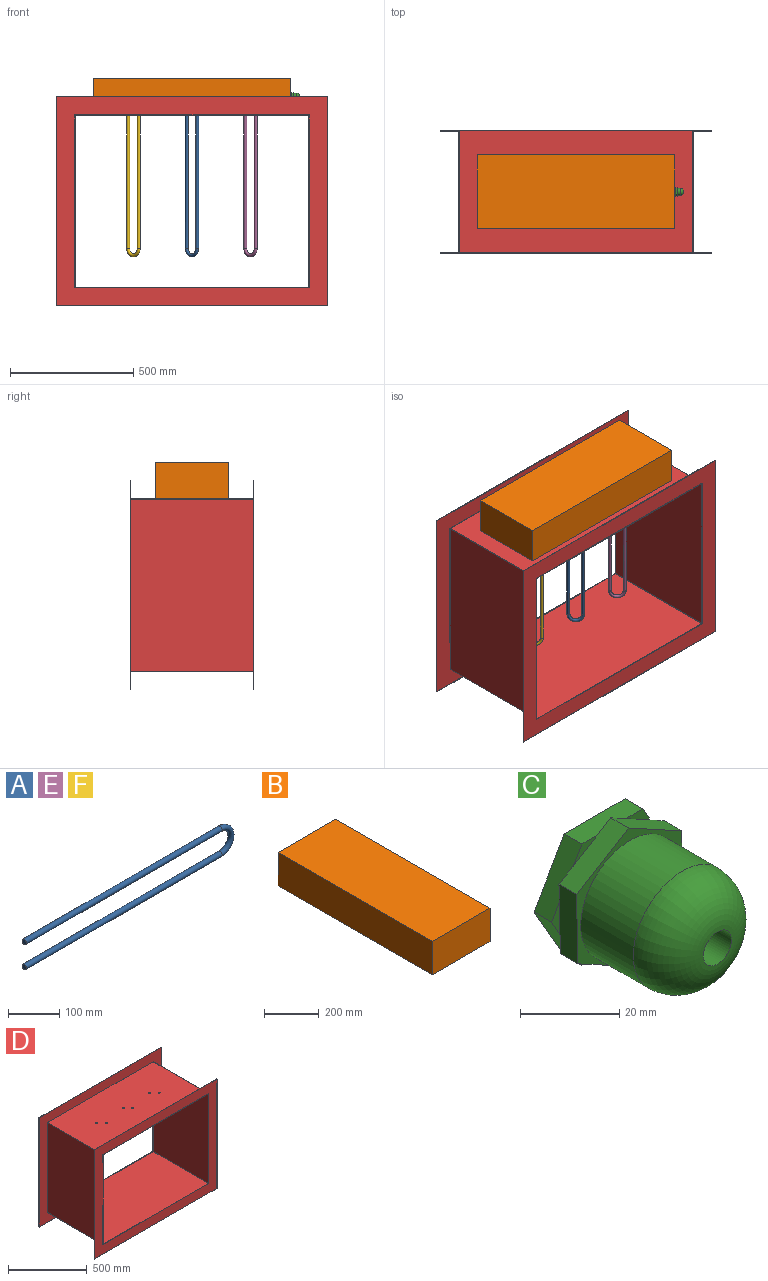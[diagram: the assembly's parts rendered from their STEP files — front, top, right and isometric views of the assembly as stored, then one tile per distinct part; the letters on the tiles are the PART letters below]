
ASSEMBLY  parts=6 mates=5
PART A: 5 faces, bbox 579x12x77.9 mm
  f0: plane 12x12mm, normal (-1,0,0), area 113.1mm2, adj f4
  f1: plane 12x12mm, normal (-1,0,0), area 113.1mm2, adj f2
  f2: cylinder r=6mm len=540mm, axis (-1,0,0), area 20357.5mm2, adj f1,f3
  f3: torus R=30mm, axis (0,-1,0), area 3553.1mm2, adj f2,f4
  f4: cylinder r=6mm len=540mm, axis (1,0,0), area 20357.5mm2, adj f0,f3
PART B: 6 faces, bbox 300x800x150 mm
  f0: plane 800x150mm, normal (-1,0,0), area 120000mm2, adj f1,f3,f4,f5
  f1: plane 800x300mm, normal (0,0,-1), area 240000mm2, adj f0,f2,f4,f5
  f2: plane 800x150mm, normal (1,0,0), area 120000mm2, adj f1,f3,f4,f5
  f3: plane 800x300mm, normal (0,0,1), area 240000mm2, adj f0,f2,f4,f5
  f4: plane 300x150mm, normal (0,-1,0), area 45000mm2, adj f0,f1,f2,f3
  f5: plane 300x150mm, normal (0,1,0), area 45000mm2, adj f0,f1,f2,f3
PART C: 29 faces, bbox 34.6x35x34.6 mm
  f0: plane 7.05x3.86mm, normal (0,-1,0), area 9.3mm2, adj f5,f6,f19
  f1: plane 8.04x2.41mm, normal (0,-1,0), area 9.3mm2, adj f5,f10,f24
  f2: plane 6.87x4.18mm, normal (0,-1,0), area 9.3mm2, adj f9,f10,f23
  f3: plane 7.05x3.86mm, normal (0,-1,0), area 9.3mm2, adj f8,f9,f22
  f4: plane 8.04x2.41mm, normal (0,-1,0), area 9.3mm2, adj f7,f8,f21
  f5: plane 15x8.66mm, normal (0.87,0,0.5), area 86.6mm2, adj f0,f1,f6,f10,f12,f13
  f6: plane 17.32x5mm, normal (0,0,1), area 86.6mm2, adj f0,f5,f7,f11,f12,f14
  f7: plane 15x8.66mm, normal (-0.87,0,0.5), area 86.6mm2, adj f4,f6,f8,f11,f12,f15
  f8: plane 15x8.66mm, normal (-0.87,0,-0.5), area 86.6mm2, adj f3,f4,f7,f9,f12,f16
  f9: plane 17.32x5mm, normal (0,0,-1), area 86.6mm2, adj f2,f3,f8,f10,f12,f17
  f10: plane 15x8.66mm, normal (0.87,0,-0.5), area 86.6mm2, adj f1,f2,f5,f9,f12,f18
  f11: plane 6.87x4.18mm, normal (0,-1,0), area 9.3mm2, adj f6,f7,f20
  f12: plane 34.64x30mm, normal (0,1,0), area 729.2mm2, adj f5,f6,f7,f8,f9,f10,f28
  f13: plane 6.96x4.02mm, normal (0,1,0), area 9.3mm2, adj f5,f19,f24
  f14: plane 8.04x2.32mm, normal (0,1,0), area 9.3mm2, adj f6,f19,f20
  f15: plane 6.96x4.12mm, normal (0,1,0), area 9.3mm2, adj f7,f20,f21
  f16: plane 6.96x4.02mm, normal (0,1,0), area 9.3mm2, adj f8,f21,f22
  f17: plane 8.04x2.32mm, normal (0,1,0), area 9.3mm2, adj f9,f22,f23
  f18: plane 6.96x4.12mm, normal (0,1,0), area 9.3mm2, adj f10,f23,f24
  f19: plane 15.2x8.31mm, normal (0.48,0,0.88), area 86.6mm2, adj f0,f13,f14,f20,f24,f25
  f20: plane 14.79x9.01mm, normal (-0.52,0,0.85), area 86.6mm2, adj f11,f14,f15,f19,f21,f25
  f21: plane 17.32x5mm, normal (-1,0,-0.02), area 86.6mm2, adj f4,f15,f16,f20,f22,f25
  f22: plane 15.2x8.31mm, normal (-0.48,0,-0.88), area 86.6mm2, adj f3,f16,f17,f21,f23,f25
  f23: plane 14.79x9.01mm, normal (0.52,0,-0.85), area 86.6mm2, adj f2,f17,f18,f22,f24,f25
  f24: plane 17.32x5mm, normal (1,0,0.02), area 86.6mm2, adj f1,f13,f18,f19,f23,f25
  f25: plane 34.63x30.39mm, normal (0,-1,0), area 163.7mm2, adj f19,f20,f21,f22,f23,f24,f26
  f26: cylinder r=14mm len=28mm, axis (0,1,0), area 1319.5mm2, adj f25,f27
  f27: torus R=4mm, axis (0,-1,0), area 1023.1mm2, adj f26,f28
  f28: cylinder r=4mm len=35mm, axis (0,-1,0), area 879.6mm2, adj f12,f27
PART D: 26 faces, bbox 1100x500x850 mm
  f0: plane 950x496mm, normal (0,0,1), area 470521.4mm2, adj f1,f7,f13,f19,f20,f21,f22,f23
  f1: plane 700x496mm, normal (-1,0,0), area 347200mm2, adj f0,f2,f13,f19
  f2: plane 950x496mm, normal (0,0,-1), area 471200mm2, adj f1,f7,f13,f19
  f3: plane 698x500mm, normal (-1,0,0), area 349000mm2, adj f4,f6,f8,f14
  f4: plane 948x500mm, normal (0,0,1), area 474000mm2, adj f3,f5,f8,f14
  f5: plane 698x500mm, normal (1,0,0), area 349000mm2, adj f4,f6,f8,f14
  f6: plane 948x500mm, normal (0,0,-1), area 473321.4mm2, adj f3,f5,f8,f14,f20,f21,f22,f23
  f7: plane 700x496mm, normal (1,0,0), area 347200mm2, adj f0,f2,f13,f19
  f8: plane 1100x850mm, normal (0,1,0), area 273296mm2, adj f3,f4,f5,f6,f9,f10,f11,f12
  f9: plane 1100x2mm, normal (0,0,1), area 2200mm2, adj f8,f10,f12,f13
  f10: plane 850x2mm, normal (-1,0,0), area 1700mm2, adj f8,f9,f11,f13
  f11: plane 1100x2mm, normal (0,0,-1), area 2200mm2, adj f8,f10,f12,f13
  f12: plane 850x2mm, normal (1,0,0), area 1700mm2, adj f8,f9,f11,f13
  f13: plane 1100x850mm, normal (0,-1,0), area 270000mm2, adj f0,f1,f2,f7,f9,f10,f11,f12
  f14: plane 1100x850mm, normal (0,-1,0), area 273296mm2, adj f3,f4,f5,f6,f15,f16,f17,f18
  f15: plane 1100x2mm, normal (0,0,1), area 2200mm2, adj f14,f16,f18,f19
  f16: plane 850x2mm, normal (-1,0,0), area 1700mm2, adj f14,f15,f17,f19
  f17: plane 1100x2mm, normal (0,0,-1), area 2200mm2, adj f14,f16,f18,f19
  f18: plane 850x2mm, normal (1,0,0), area 1700mm2, adj f14,f15,f17,f19
  f19: plane 1100x850mm, normal (0,1,0), area 270000mm2, adj f0,f1,f2,f7,f15,f16,f17,f18
  f20: cylinder r=6mm len=12mm, axis (0,0,1), area 37.7mm2, adj f0,f6
  f21: cylinder r=6mm len=12mm, axis (0,0,1), area 37.7mm2, adj f0,f6
  f22: cylinder r=6mm len=12mm, axis (0,0,1), area 37.7mm2, adj f0,f6
  f23: cylinder r=6mm len=12mm, axis (0,0,1), area 37.7mm2, adj f0,f6
  f24: cylinder r=6mm len=12mm, axis (0,0,1), area 37.7mm2, adj f0,f6
  f25: cylinder r=6mm len=12mm, axis (0,0,1), area 37.7mm2, adj f0,f6
PART E: same geometry as A
PART F: same geometry as A
PLACE A rot(axis=(-0.68,0.28,0.68),148.6deg) t=(624.37,202.93,-72.53)mm
PLACE B rot(axis=(0,0,-1),90deg) t=(1045.62,339.25,-72.53)mm
PLACE C rot(axis=(0.58,-0.58,0.58),120deg) t=(1045.62,189.25,2.47)mm
PLACE D rot(axis=(-0.95,-0.3,0),0deg) t=(645.62,439.25,-441.6)mm
PLACE E rot(axis=(-0.68,0.28,0.68),148.6deg) t=(861.87,202.43,-72.53)mm
PLACE F rot(axis=(-0.68,0.28,0.68),149deg) t=(386.6,202.07,-72.53)mm
MATE revolute E.f4 <-> D.f20  axis (0,0,-1) through (904.29,168.49,-72.53)mm
MATE fastened B.f1 <-> D.f0  axis (0,0,-1) through (645.62,189.25,-72.53)mm
MATE revolute F.f4 <-> D.f24  axis (0,0,1) through (429.38,168.58,-72.53)mm
MATE fastened C.f26 <-> B.f5  axis (-1,0,0) through (1045.62,189.25,2.47)mm
MATE revolute A.f4 <-> D.f22  axis (0,0,1) through (666.79,168.99,-72.53)mm
